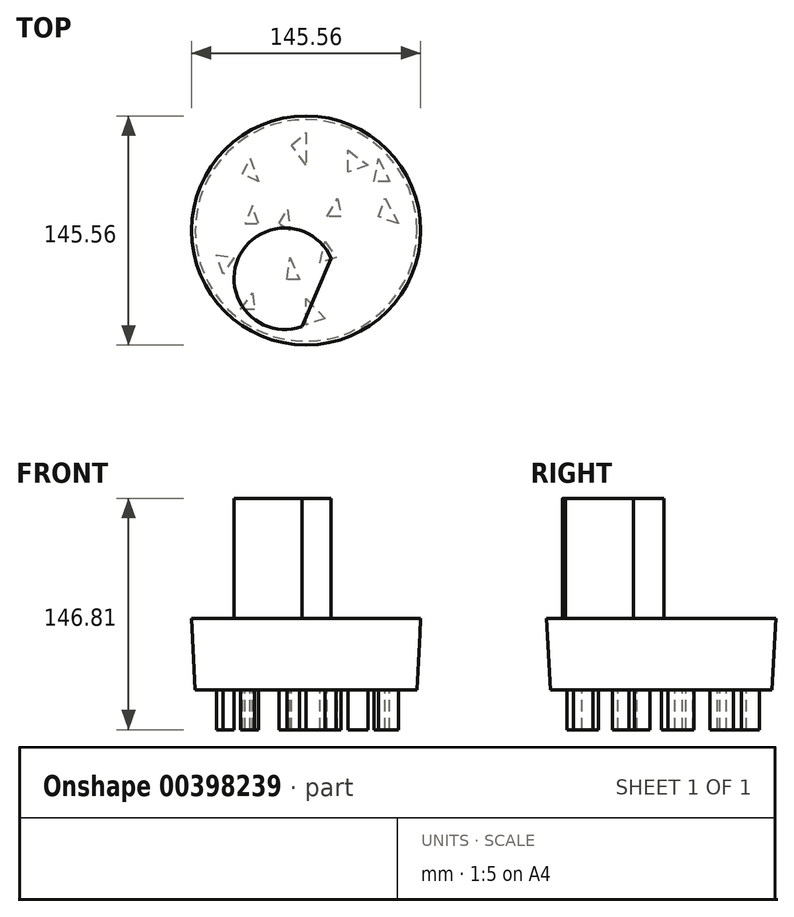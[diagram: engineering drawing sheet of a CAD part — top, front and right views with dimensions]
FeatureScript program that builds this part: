
annotation { "Feature Type Name" : "Feature", "Feature Type Description" : "" }
export const myFeature = defineFeature(function(context is Context, id is Id, definition is map)
    precondition{}
    {
        {
            var Q0;
            Q0=qCreatedBy(makeId("Top.planeOp"),FACE);
            var sketch = newSketch(context, id + "F0", { "sketchPlane" : qUnion([Q0])});
            skCircle(sketch, "E0", {"center": v(0, 0) * mm, "radius": 70.4 * mm});
            skSolve(sketch);
        }
        {
            var Q0;
            Q0 = qSketchRegion(id + "F0", true);
            extrude(context, id + "F1", {"entities" : qUnion([Q0]), "depth" : 45.2 * mm, "hasDraft" : true, "draftAngle" : 3 * degree});
        }
        {
            var Q0;
            Q0=makeQuery(id+"F0.imprint","IMPRINT",FACE,{"disambiguationData":[TD([[makeQuery(id+"F0.imprint","IMPRINT",EDGE,{"derivedFrom":sQuery(id+"F0.wireOp",EDGE,"E0")}),1.0]])]});
            var sketch = newSketch(context, id + "F2", { "sketchPlane" : qUnion([Q0])});
            skLineSegment(sketch, "E1", {"start": v(50.47, -33.67) * mm, "end": v(38.18, -33.67) * mm});
            skLineSegment(sketch, "E2", {"start": v(38.18, -33.67) * mm, "end": v(45.43, -19.58) * mm});
            skLineSegment(sketch, "E3", {"start": v(45.43, -19.58) * mm, "end": v(50.47, -33.67) * mm});
            skSolve(sketch);
        }
        {
            var Q0;
            Q0=makeQuery(id+"F2.imprint","IMPRINT",FACE,{"disambiguationData":[TD([[makeQuery(id+"F2.imprint","IMPRINT",EDGE,{"derivedFrom":sQuery(id+"F2.wireOp",EDGE,"E1")}),1.0]])]});
            var sketch = newSketch(context, id + "F3", { "sketchPlane" : qUnion([Q0])});
            skLineSegment(sketch, "E4", {"start": v(22.19, 8.68) * mm, "end": v(13.27, 8.68) * mm});
            skLineSegment(sketch, "E5", {"start": v(13.27, 8.68) * mm, "end": v(20, 20.26) * mm});
            skLineSegment(sketch, "E6", {"start": v(20, 20.26) * mm, "end": v(22.19, 8.68) * mm});
            skLineSegment(sketch, "E7", {"start": v(39.37, 41.38) * mm, "end": v(26.72, 37.13) * mm});
            skLineSegment(sketch, "E8", {"start": v(26.72, 37.13) * mm, "end": v(26.72, 50.96) * mm});
            skLineSegment(sketch, "E9", {"start": v(26.72, 50.96) * mm, "end": v(39.37, 41.38) * mm});
            skLineSegment(sketch, "E10", {"start": v(0, 62.23) * mm, "end": v(0, 41.38) * mm});
            skLineSegment(sketch, "E11", {"start": v(0, 41.38) * mm, "end": v(-9.29, 54.09) * mm});
            skLineSegment(sketch, "E12", {"start": v(-9.29, 54.09) * mm, "end": v(0, 62.23) * mm});
            skLineSegment(sketch, "E13", {"start": v(-10.14, 0) * mm, "end": v(-17.22, 4.22) * mm});
            skLineSegment(sketch, "E14", {"start": v(-17.22, 4.22) * mm, "end": v(-11.73, 13.41) * mm});
            skLineSegment(sketch, "E15", {"start": v(-11.73, 13.41) * mm, "end": v(-10.14, 0) * mm});
            skLineSegment(sketch, "E16", {"start": v(-4.34, -31.05) * mm, "end": v(-12.09, -31.05) * mm});
            skLineSegment(sketch, "E17", {"start": v(-12.09, -31.05) * mm, "end": v(-10.14, -17.06) * mm});
            skLineSegment(sketch, "E18", {"start": v(-10.14, -17.06) * mm, "end": v(-4.34, -31.05) * mm});
            skLineSegment(sketch, "E19", {"start": v(12, -55.94) * mm, "end": v(0, -59.98) * mm});
            skLineSegment(sketch, "E20", {"start": v(0, -59.98) * mm, "end": v(0, -43.24) * mm});
            skLineSegment(sketch, "E21", {"start": v(0, -43.24) * mm, "end": v(12, -55.94) * mm});
            skLineSegment(sketch, "E22", {"start": v(58.58, 4.22) * mm, "end": v(45.9, 8.68) * mm});
            skLineSegment(sketch, "E23", {"start": v(45.9, 8.68) * mm, "end": v(50.12, 20.7) * mm});
            skLineSegment(sketch, "E24", {"start": v(50.12, 20.7) * mm, "end": v(58.58, 4.22) * mm});
            skLineSegment(sketch, "E25", {"start": v(-30.28, 30.97) * mm, "end": v(-40.4, 35.75) * mm});
            skLineSegment(sketch, "E26", {"start": v(-40.4, 35.75) * mm, "end": v(-35.51, 46.1) * mm});
            skLineSegment(sketch, "E27", {"start": v(-35.51, 46.1) * mm, "end": v(-30.28, 30.97) * mm});
            skLineSegment(sketch, "E28", {"start": v(-45.72, -17.19) * mm, "end": v(-52.94, -27.6) * mm});
            skLineSegment(sketch, "E29", {"start": v(-52.94, -27.6) * mm, "end": v(-56.98, -15.6) * mm});
            skLineSegment(sketch, "E30", {"start": v(-56.98, -15.6) * mm, "end": v(-45.72, -17.19) * mm});
            skLineSegment(sketch, "E31", {"start": v(19.07, -17.19) * mm, "end": v(8.7, -20.67) * mm});
            skLineSegment(sketch, "E32", {"start": v(8.7, -20.67) * mm, "end": v(12, -7.11) * mm});
            skLineSegment(sketch, "E33", {"start": v(12, -7.11) * mm, "end": v(19.07, -17.19) * mm});
            skLineSegment(sketch, "E34", {"start": v(-30.28, 4.22) * mm, "end": v(-34.13, 15.68) * mm});
            skLineSegment(sketch, "E35", {"start": v(-34.13, 15.68) * mm, "end": v(-38.8, 4.22) * mm});
            skLineSegment(sketch, "E36", {"start": v(-38.8, 4.22) * mm, "end": v(-30.28, 4.22) * mm});
            skLineSegment(sketch, "E37", {"start": v(-32.62, -50.34) * mm, "end": v(-41.78, -50.34) * mm});
            skLineSegment(sketch, "E38", {"start": v(-41.78, -50.34) * mm, "end": v(-34.1, -39.9) * mm});
            skLineSegment(sketch, "E39", {"start": v(-34.1, -39.9) * mm, "end": v(-32.62, -50.34) * mm});
            skLineSegment(sketch, "E40", {"start": v(53.04, 30.97) * mm, "end": v(43.17, 30.97) * mm});
            skLineSegment(sketch, "E41", {"start": v(43.17, 30.97) * mm, "end": v(45.91, 45.8) * mm});
            skLineSegment(sketch, "E42", {"start": v(45.91, 45.8) * mm, "end": v(53.04, 30.97) * mm});
            skSolve(sketch);
        }
        {
            var Q0;
            Q0 = qSketchRegion(id + "F3", true);
            extrude(context, id + "F4", {"entities" : qUnion([Q0]), "operationType" : NewBodyOperationType.ADD, "oppositeDirection" : true, "depth" : 25.4 * mm});
        }
        {
            var Q0;
            Q0=makeQuery(id+"F1.opExtrude","CAP_FACE",FACE,{"disambiguationData":[OSD([sQuery(id+"F0.wireOp",EDGE,"E0")])],"isStart":false});
            var sketch = newSketch(context, id + "F5", { "sketchPlane" : qUnion([Q0])});
            skArc(sketch, "E43", {"start": v(15.94, -17.78) * mm, "mid": v(-43.17, -17.9) * mm, "end": v(-2.7, -61) * mm});
            skLineSegment(sketch, "E44", {"start": v(-2.7, -61) * mm, "end": v(15.94, -17.78) * mm});
            skSolve(sketch);
        }
        {
            var Q0;
            Q0 = qSketchRegion(id + "F5", true);
            extrude(context, id + "F6", {"entities" : qUnion([Q0]), "operationType" : NewBodyOperationType.ADD, "depth" : 76.2 * mm, "offsetDistance" : 25.4 * mm});
        }
    });
